# Revit family: Safety-Equipment_Door-Frame-Protection_Omega-Industrial_Trak-Shield
name_source: partatom
category: Generic Models
units: mm (PartAtom-declared; Revit-internal decimal feet)

## family parameters
Always vertical = Yes
Can host rebar = No
Classification Number = 23.30.80.17
Cut with Voids When Loaded = No
Maintain Annotation Orientation = No
Part Type = Normal
Room Calculation Point = No
Round Connector Dimension = Use Diameter
Shared = No
Work Plane-Based = Yes

## types (1)
- Trak Shield - 48
    Assembly Code = E1090
    Base Plate Material = Omega_1/2 in Steel
    Default Elevation = 4' - 0"
    Description = Overhead Door Track Guard
    Expected Lifespan (Years) = 25
    Guard Material = Omega_7 Ga. Steel
    Installation Phase = Industrial Safety Equipment
    Keynote = 41 67 19
    Maintenance Schedule (Months) = 0
    Manufacturer = Omega Industrial Products, Inc.
    Manufacturer Fax = 262-284-4199
    Manufacturer Website = https://www.omegaindl.com
    Model = OM8048
    Product Data = https://www.arcat.com
    Product Properties = https://www.omegaindl.com
    Revision = R0_06-2018
    Sales Information = https://www.omegaindl.com
    Send Message = https://www.omegaindl.com
    Specification = https://www.arcat.com
    URL = https://www.arcat.com
    Unit Depth = 0' - 10"
    Unit Height = 4' - 0"
    Unit Width = 0' - 10"
    Warranty Duration (Years) = 0

## geometry (parser evidence)
native form markers: Blend x42, Sweep x2
no freeform markers — native parametric forms only
